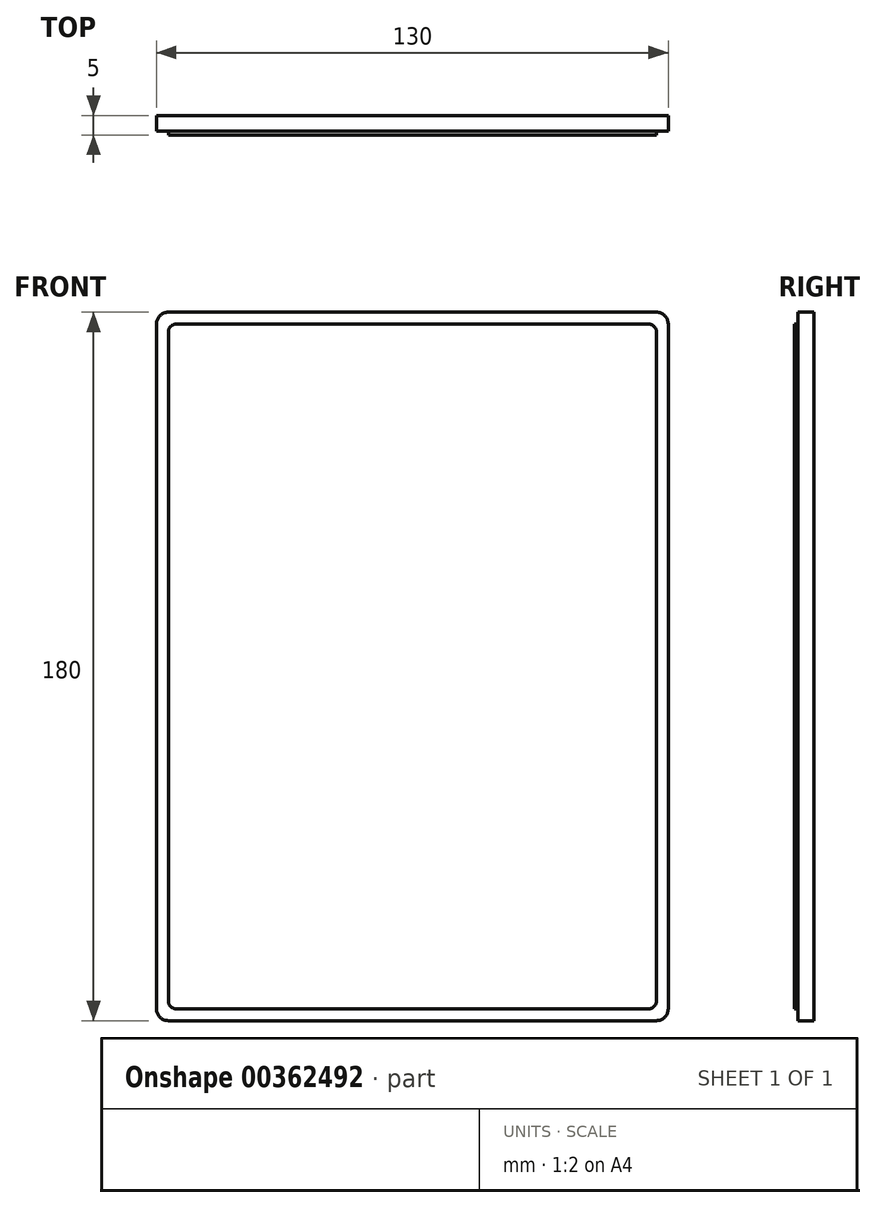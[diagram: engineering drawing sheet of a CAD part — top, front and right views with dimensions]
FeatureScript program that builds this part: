
annotation { "Feature Type Name" : "Feature", "Feature Type Description" : "" }
export const myFeature = defineFeature(function(context is Context, id is Id, definition is map)
    precondition{}
    {
        {
            var Q0;
            Q0=qCreatedBy(makeId("Front.planeOp"),FACE);
            var sketch = newSketch(context, id + "F0", { "sketchPlane" : qUnion([Q0])});
            skLineSegment(sketch, "E0.bottom", {"start": v(-82.66, 125.97) * mm, "end": v(47.34, 125.97) * mm});
            skLineSegment(sketch, "E0.top", {"start": v(-82.66, -54.03) * mm, "end": v(47.34, -54.03) * mm});
            skLineSegment(sketch, "E0.left", {"start": v(-82.66, 125.97) * mm, "end": v(-82.66, -54.03) * mm});
            skLineSegment(sketch, "E0.right", {"start": v(47.34, 125.97) * mm, "end": v(47.34, -54.03) * mm});
            skSolve(sketch);
        }
        {
            var Q0;
            Q0=makeQuery(id+"F0.imprint","IMPRINT",FACE,{"disambiguationData":[TD([[makeQuery(id+"F0.imprint","IMPRINT",EDGE,{"derivedFrom":sQuery(id+"F0.wireOp",EDGE,"E0.bottom")}),-1.0]])]});
            extrude(context, id + "F1", {"entities" : qUnion([Q0]), "depth" : 4 * mm});
        }
        {
            var Q0;
            Q0=makeQuery(id+"F1.opExtrude","SWEPT_EDGE",EDGE,{"disambiguationData":[OSD([sQuery(id+"F0.wireOp",EDGE,"E0.bottom"),sQuery(id+"F0.wireOp",EDGE,"E0.left")])]});
            var Q1;
            Q1=makeQuery(id+"F1.opExtrude","SWEPT_EDGE",EDGE,{"disambiguationData":[OSD([sQuery(id+"F0.wireOp",EDGE,"E0.top"),sQuery(id+"F0.wireOp",EDGE,"E0.left")])]});
            var Q2;
            Q2=makeQuery(id+"F1.opExtrude","SWEPT_EDGE",EDGE,{"disambiguationData":[OSD([sQuery(id+"F0.wireOp",EDGE,"E0.top"),sQuery(id+"F0.wireOp",EDGE,"E0.right")])]});
            var Q3;
            Q3=makeQuery(id+"F1.opExtrude","SWEPT_EDGE",EDGE,{"disambiguationData":[OSD([sQuery(id+"F0.wireOp",EDGE,"E0.bottom"),sQuery(id+"F0.wireOp",EDGE,"E0.right")])]});
            fillet(context, id + "F2", {"entities" : qUnion([Q0, Q1, Q2, Q3]), "radius" : 3 * mm, "tangentPropagation" : true, "allowEdgeOverflow" : false});
        }
        {
            var Q0;
            Q0=makeQuery(id+"F1.opExtrude","CAP_FACE",FACE,{"disambiguationData":[OSD([sQuery(id+"F0.wireOp",EDGE,"E0.bottom"),sQuery(id+"F0.wireOp",EDGE,"E0.top"),sQuery(id+"F0.wireOp",EDGE,"E0.left"),sQuery(id+"F0.wireOp",EDGE,"E0.right")])],"isStart":false});
            var sketch = newSketch(context, id + "F3", { "sketchPlane" : qUnion([Q0])});
            skLineSegment(sketch, "E1.0", {"start": v(-79.66, 122.97) * mm, "end": v(-79.66, -51.03) * mm});
            skLineSegment(sketch, "E1.1", {"start": v(44.34, 122.97) * mm, "end": v(-79.66, 122.97) * mm});
            skLineSegment(sketch, "E1.2", {"start": v(44.34, -51.03) * mm, "end": v(44.34, 122.97) * mm});
            skLineSegment(sketch, "E1.3", {"start": v(-79.66, -51.03) * mm, "end": v(44.34, -51.03) * mm});
            skSolve(sketch);
        }
        {
            var Q0;
            Q0 = qSketchRegion(id + "F3", true);
            extrude(context, id + "F4", {"entities" : qUnion([Q0]), "operationType" : NewBodyOperationType.ADD, "depth" : 1 * mm});
        }
        {
            var Q0;
            Q0=makeQuery(id+"F4.opExtrude","SWEPT_EDGE",EDGE,{"disambiguationData":[OSD([sQuery(id+"F3.wireOp",EDGE,"E1.0"),sQuery(id+"F3.wireOp",EDGE,"E1.1")])]});
            var Q1;
            Q1=makeQuery(id+"F4.opExtrude","SWEPT_EDGE",EDGE,{"disambiguationData":[OSD([sQuery(id+"F3.wireOp",EDGE,"E1.1"),sQuery(id+"F3.wireOp",EDGE,"E1.2")])]});
            var Q2;
            Q2=makeQuery(id+"F4.opExtrude","SWEPT_EDGE",EDGE,{"disambiguationData":[OSD([sQuery(id+"F3.wireOp",EDGE,"E1.0"),sQuery(id+"F3.wireOp",EDGE,"E1.3")])]});
            var Q3;
            Q3=makeQuery(id+"F4.opExtrude","SWEPT_EDGE",EDGE,{"disambiguationData":[OSD([sQuery(id+"F3.wireOp",EDGE,"E1.2"),sQuery(id+"F3.wireOp",EDGE,"E1.3")])]});
            fillet(context, id + "F5", {"entities" : qUnion([Q0, Q1, Q2, Q3]), "radius" : 2 * mm, "tangentPropagation" : true, "allowEdgeOverflow" : false});
        }
    });
